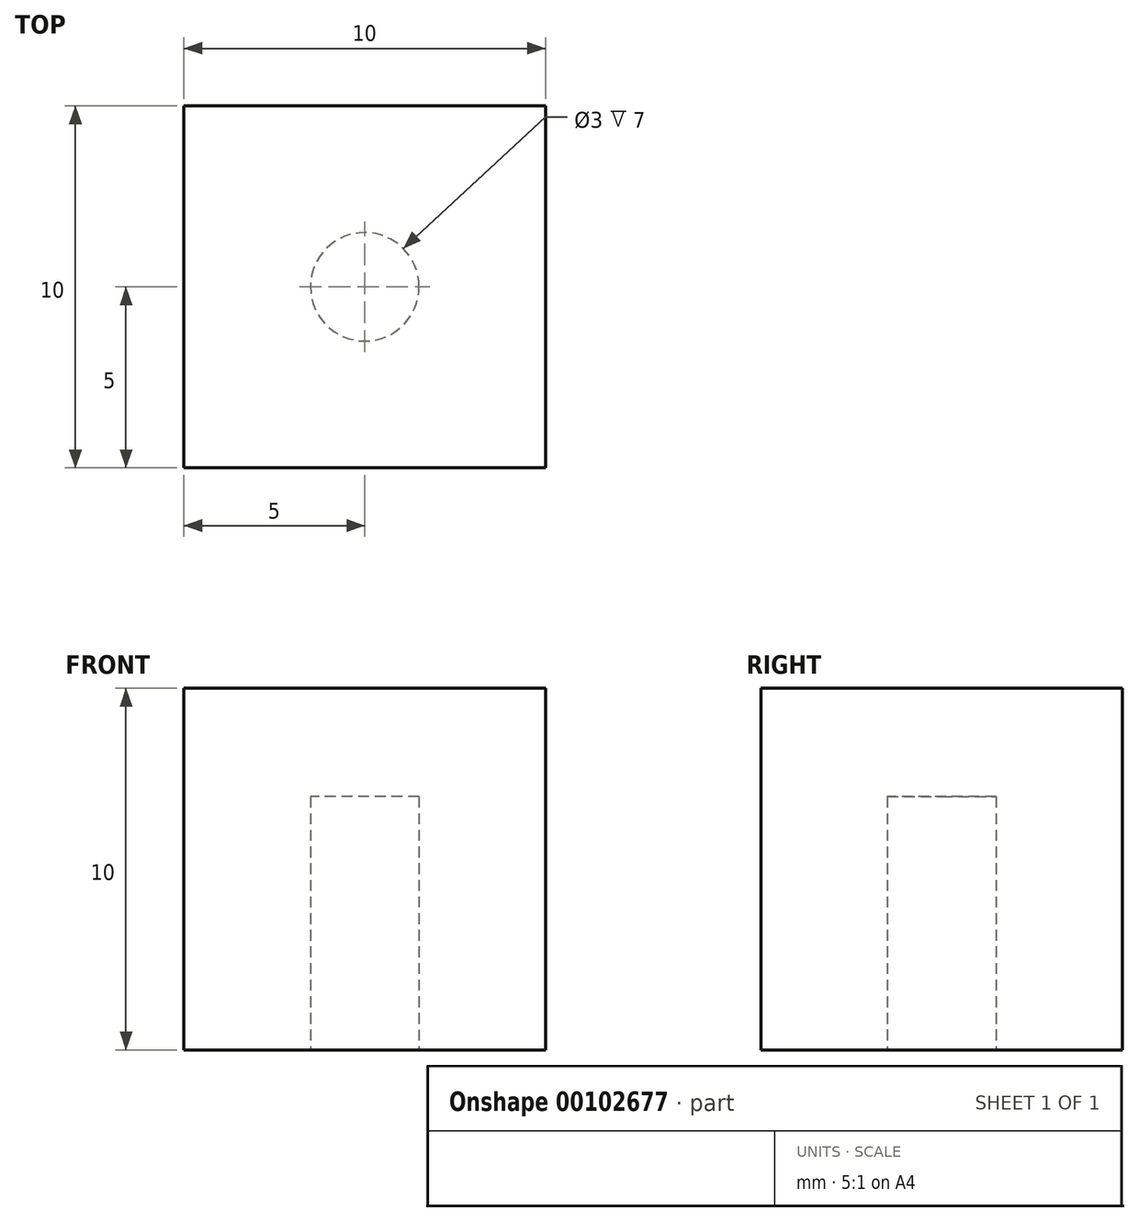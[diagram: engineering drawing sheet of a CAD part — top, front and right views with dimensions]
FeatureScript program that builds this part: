
annotation { "Feature Type Name" : "Feature", "Feature Type Description" : "" }
export const myFeature = defineFeature(function(context is Context, id is Id, definition is map)
    precondition{}
    {
        {
            var Q0;
            Q0=qCreatedBy(makeId("Top.planeOp"),FACE);
            var sketch = newSketch(context, id + "F0", { "sketchPlane" : qUnion([Q0])});
            skLineSegment(sketch, "E0.bottom", {"start": v(5, -5) * mm, "end": v(-5, -5) * mm});
            skLineSegment(sketch, "E0.top", {"start": v(5, 5) * mm, "end": v(-5, 5) * mm});
            skLineSegment(sketch, "E0.left", {"start": v(5, -5) * mm, "end": v(5, 5) * mm});
            skLineSegment(sketch, "E0.right", {"start": v(-5, -5) * mm, "end": v(-5, 5) * mm});
            skPoint(sketch, "E0.middle", {"position": v(0, 0) * mm});
            skCircle(sketch, "E1", {"center": v(0, 0) * mm, "radius": 1.5 * mm});
            skSolve(sketch);
        }
        {
            var Q0;
            Q0=makeQuery(id+"F0.imprint","IMPRINT",FACE,{"disambiguationData":[TD([[makeQuery(id+"F0.imprint","IMPRINT",EDGE,{"derivedFrom":sQuery(id+"F0.wireOp",EDGE,"E0.bottom")}),-1.0]])]});
            var Q1;
            Q1=makeQuery(id+"F0.imprint","IMPRINT",FACE,{"disambiguationData":[TD([[makeQuery(id+"F0.imprint","IMPRINT",EDGE,{"derivedFrom":sQuery(id+"F0.wireOp",EDGE,"E1")}),1.0]])]});
            extrude(context, id + "F1", {"entities" : qUnion([Q0, Q1]), "depth" : 10 * mm});
        }
        {
            var Q0;
            Q0=makeQuery(id+"F0.imprint","IMPRINT",FACE,{"disambiguationData":[TD([[makeQuery(id+"F0.imprint","IMPRINT",EDGE,{"derivedFrom":sQuery(id+"F0.wireOp",EDGE,"E1")}),1.0]])]});
            extrude(context, id + "F2", {"entities" : qUnion([Q0]), "operationType" : NewBodyOperationType.REMOVE, "depth" : 7 * mm});
        }
    });
